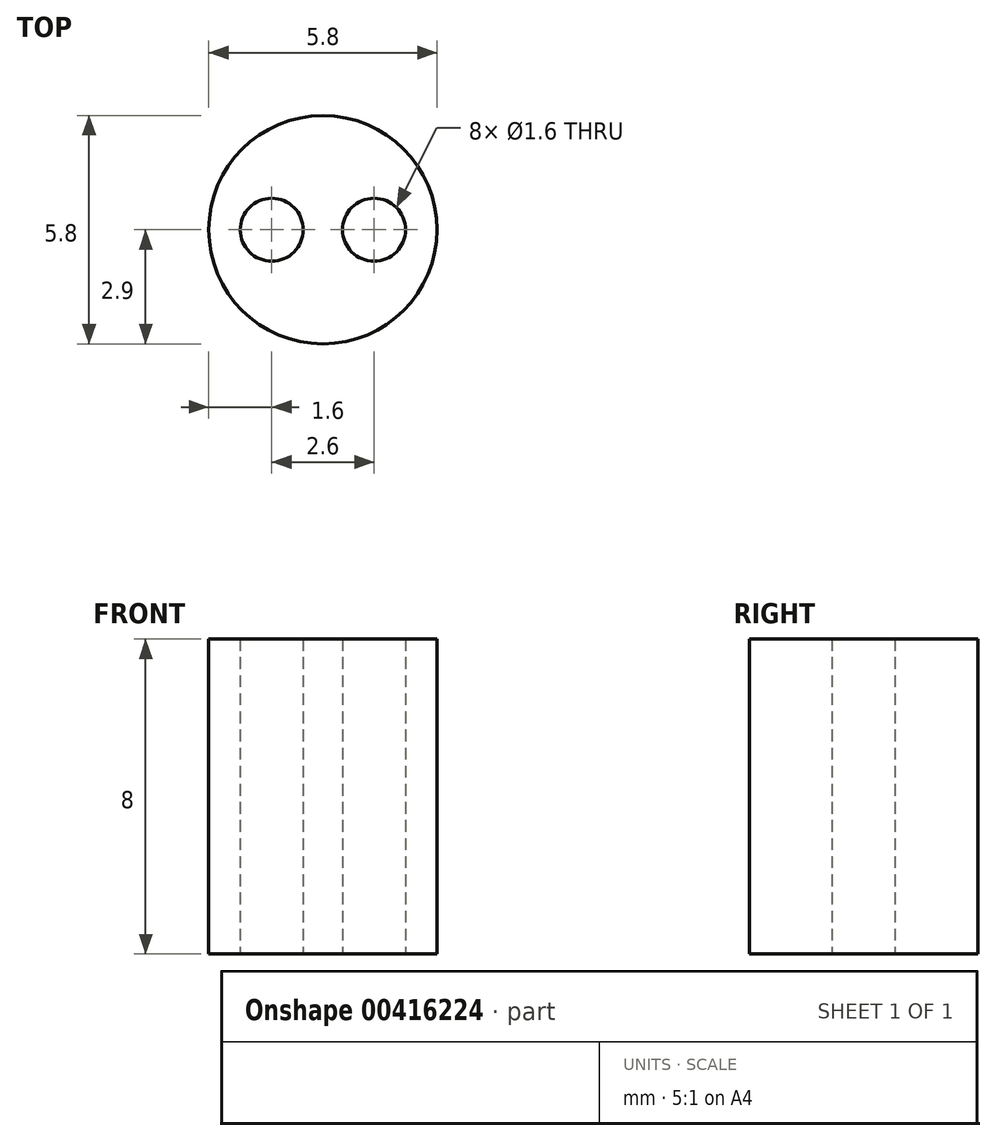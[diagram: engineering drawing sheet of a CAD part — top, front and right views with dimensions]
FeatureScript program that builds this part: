
annotation { "Feature Type Name" : "Feature", "Feature Type Description" : "" }
export const myFeature = defineFeature(function(context is Context, id is Id, definition is map)
    precondition{}
    {
        {
            var Q0;
            Q0=qCreatedBy(makeId("Top.planeOp"),FACE);
            var sketch = newSketch(context, id + "F0", { "sketchPlane" : qUnion([Q0])});
            skCircle(sketch, "E0", {"center": v(0, 0) * mm, "radius": 2.9 * mm});
            skLineSegment(sketch, "E1", {"start": v(1.3, 0) * mm, "end": v(-1.3, 0) * mm, "construction": true});
            skCircle(sketch, "E2", {"center": v(1.3, 0) * mm, "radius": 0.8 * mm});
            skCircle(sketch, "E3", {"center": v(-1.3, 0) * mm, "radius": 0.8 * mm});
            skSolve(sketch);
        }
        {
            var Q0;
            Q0=makeQuery(id+"F0.imprint","IMPRINT",FACE,{"disambiguationData":[TD([[makeQuery(id+"F0.imprint","IMPRINT",EDGE,{"derivedFrom":sQuery(id+"F0.wireOp",EDGE,"E0")}),1.0]])]});
            extrude(context, id + "F1", {"entities" : qUnion([Q0]), "depth" : 8 * mm, "offsetDistance" : 25 * mm});
        }
    });
